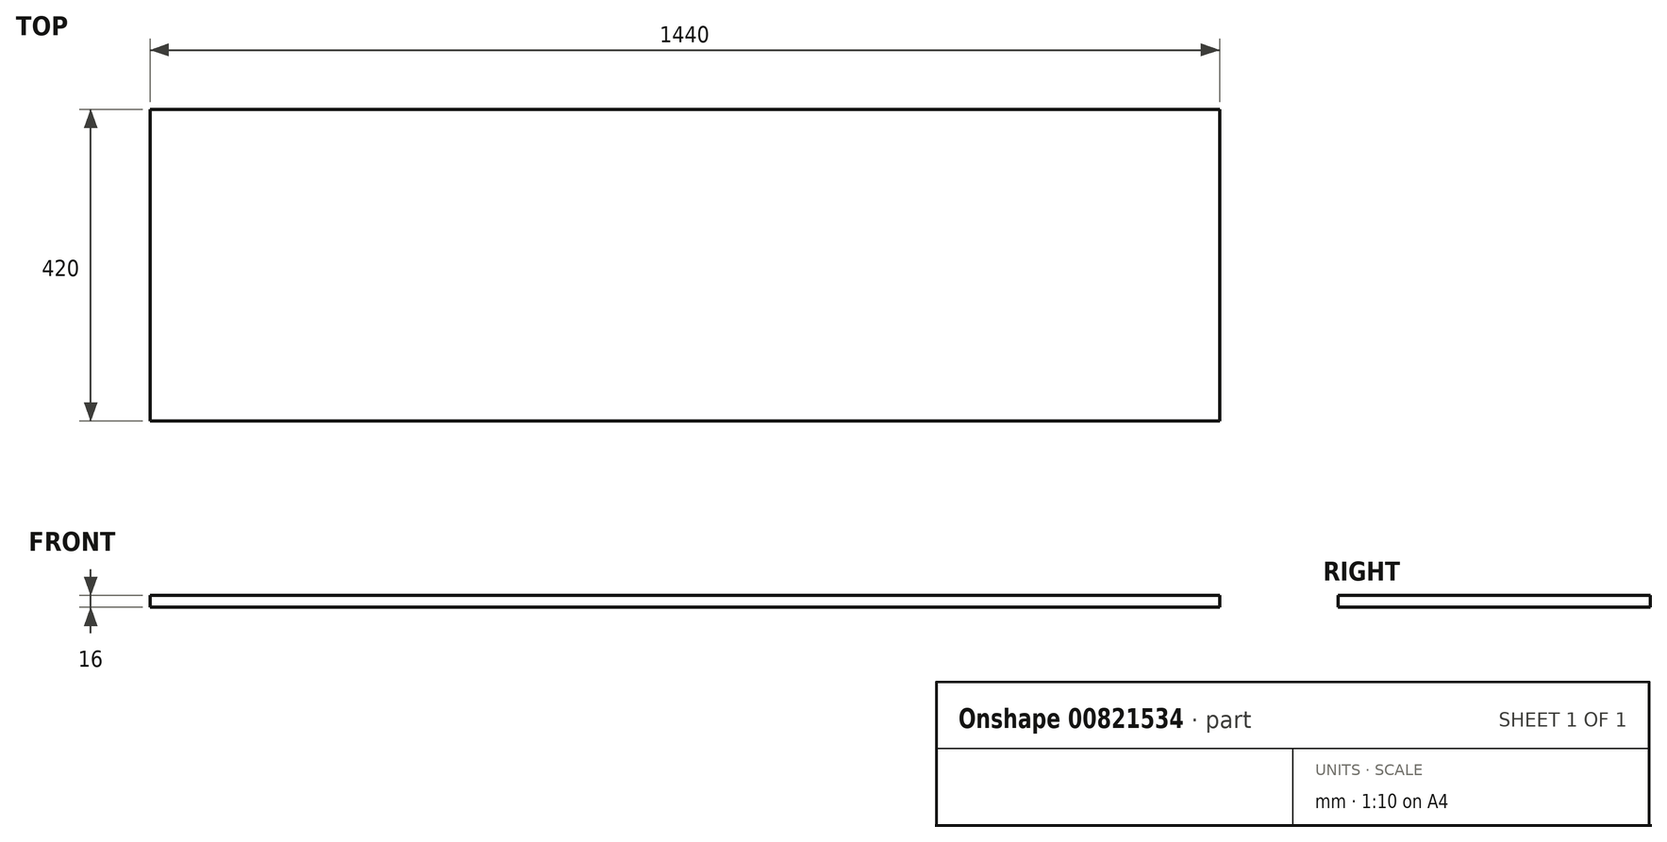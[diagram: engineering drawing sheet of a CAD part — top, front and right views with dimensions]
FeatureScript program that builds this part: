
annotation { "Feature Type Name" : "Feature", "Feature Type Description" : "" }
export const myFeature = defineFeature(function(context is Context, id is Id, definition is map)
    precondition{}
    {
        {
            var Q0;
            Q0=qCreatedBy(makeId("Top.planeOp"),FACE);
            var sketch = newSketch(context, id + "F0", { "sketchPlane" : qUnion([Q0])});
            skLineSegment(sketch, "E0.bottom", {"start": v(-720, 210) * mm, "end": v(720, 210) * mm});
            skLineSegment(sketch, "E0.top", {"start": v(-720, -210) * mm, "end": v(720, -210) * mm});
            skLineSegment(sketch, "E0.left", {"start": v(-720, 210) * mm, "end": v(-720, -210) * mm});
            skLineSegment(sketch, "E0.right", {"start": v(720, 210) * mm, "end": v(720, -210) * mm});
            skPoint(sketch, "E0.middle", {"position": v(0, 0) * mm});
            skSolve(sketch);
        }
        {
            var Q0;
            Q0=makeQuery(id+"F0.imprint","IMPRINT",FACE,{"disambiguationData":[TD([[makeQuery(id+"F0.imprint","IMPRINT",EDGE,{"derivedFrom":sQuery(id+"F0.wireOp",EDGE,"E0.bottom")}),-1.0]])]});
            extrude(context, id + "F1", {"entities" : qUnion([Q0]), "endBound" : BoundingType.SYMMETRIC, "depth" : 16 * mm, "offsetDistance" : 25 * mm});
        }
    });
